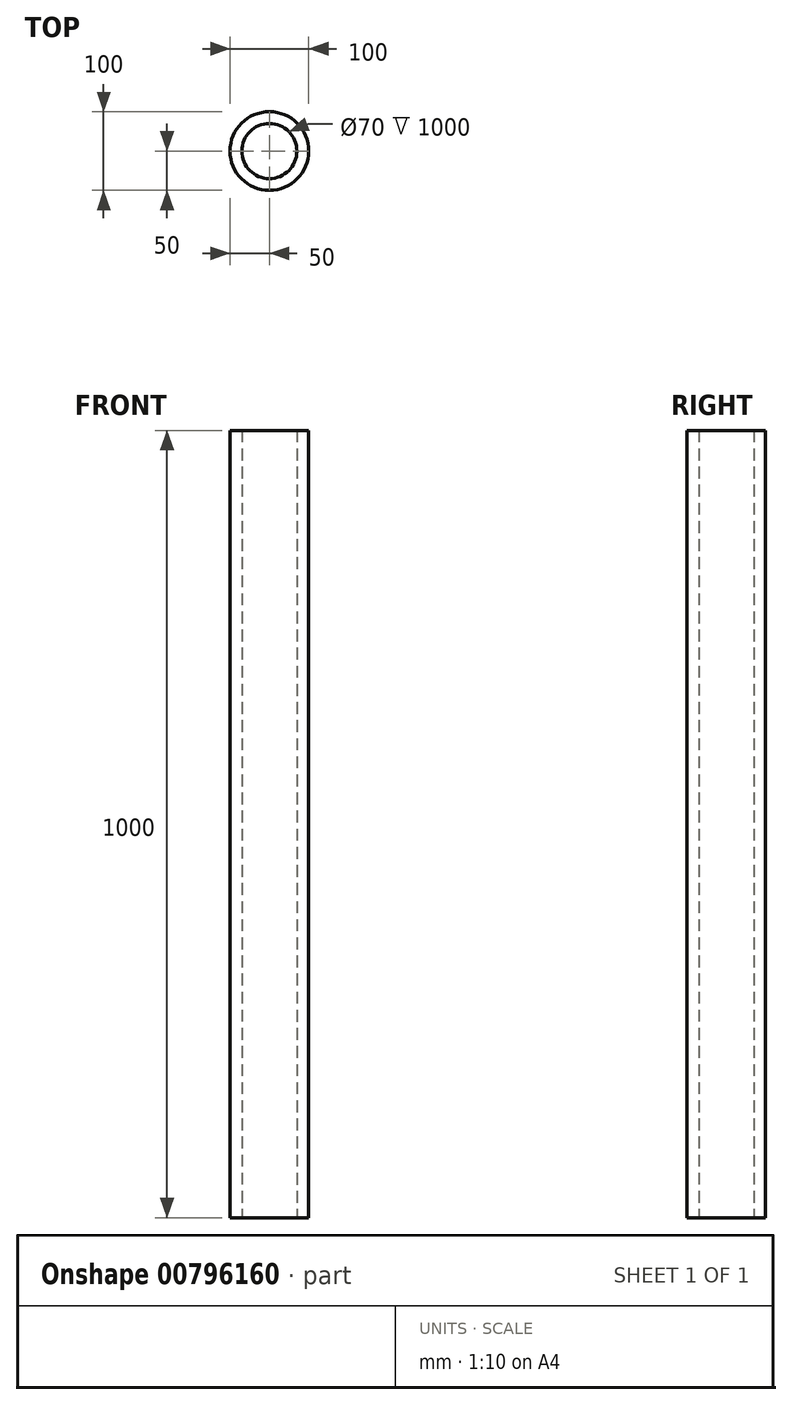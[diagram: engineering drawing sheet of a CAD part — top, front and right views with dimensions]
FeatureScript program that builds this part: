
annotation { "Feature Type Name" : "Feature", "Feature Type Description" : "" }
export const myFeature = defineFeature(function(context is Context, id is Id, definition is map)
    precondition{}
    {
        {
            var Q0;
            Q0=qCreatedBy(makeId("Top.planeOp"),FACE);
            var sketch = newSketch(context, id + "F0", { "sketchPlane" : qUnion([Q0])});
            skCircle(sketch, "E0", {"center": v(0, 0) * mm, "radius": 50 * mm});
            skCircle(sketch, "E1", {"center": v(0, 0) * mm, "radius": 35 * mm});
            skSolve(sketch);
        }
        {
            var Q0;
            Q0=makeQuery(id+"F0.imprint","IMPRINT",FACE,{"disambiguationData":[TD([[makeQuery(id+"F0.imprint","IMPRINT",EDGE,{"derivedFrom":sQuery(id+"F0.wireOp",EDGE,"E0")}),1.0]])]});
            extrude(context, id + "F1", {"entities" : qUnion([Q0]), "depth" : 1000 * mm, "offsetDistance" : 25 * mm});
        }
    });
